# Revit family: Hager-Type B SP&N Distribution Boards-Surface_mounted-IP30-With_Cover-With_DIN-Hosted-GB-en
name_source: partatom
category: Electrical Equipment
units: mm (PartAtom-declared; Revit-internal decimal feet)

## family parameters
Cut with Voids When Loaded = No
Host = Face
Maintain Annotation Orientation = Yes
Panel Configuration = Two Columns, Circuits Across
Part Type = Panelboard
Room Calculation Point = No
Round Connector Dimension = Use Diameter
Shared = No

## types (4) — shared parameters
BC_MODEL_ID = 1554195
BC_OBJECT_ID = 513819
BC_OBJECT_VERSION = #1
Code hager = ADD-EC000214_EU
EF000003 - Mounting method = Surface mounted
EF000008 - Width = 465 mm  [stored 1.52559 ft]
EF000024 - UV resistant = No
EF000049 - Depth = 165 mm  [stored 0.541339 ft]
EF000116 - RAL number = 7035
EF000118 - With mounting plate = No
EF001062 - EMC-version = No
EF001088 - Extension possible = No
EF001134 - With DIN-rail = Yes
EF002950 - Width in number of modular spacings = 16
EF005474 - Degree of protection (IP rating) = IP30
EF006244 - Transparent cover/door = No
EF006306 - With lock = No
EF015776 - Earthing terminal block = Yes
EF015777 - Neutral terminal block = Yes
EF015941 - Signal passing door = No
ETIM class code = EC000214
ETIM class name = Small distribution board
HG000001-Number of columns = 1
HG000002-With door or cover = Yes
HG000003-Range = Type B SP&N Distribution Boards
HG000005-Thickness = 2 mm  [stored 0.00656168 ft]
HG000006-Flush mounted = No
HG000009-Double swing door = No
HG000010-Asymmetric doors = No
HG000011-Empty rows from bottom = No
HG000012-Door swing angle = 90.00°
HG000013-Door on the left = No
HG000014-Door on the right = Yes
HG000015-Clearance visibility = Yes
HG000016-Door 3D visibility = Yes
HG000017-Distance between poles = 18 mm  [stored 0.0590551 ft]
HG000060-RAL-number = 7035
HG000099-Onfly Template ID = 507532
HGEF002950-Width in number of modular spacings = 16
Manufacturer = Hager
Name = Type B SP&N Distribution Boards-Surface_mounted-IP30-With_Cover-With_DIN-GB
Name BIM&CO = Electricity
Name hager = ADD_Enclosures_EC000214
Uniformat = Low Tension Service & Dist.
Uniformat code = D501001
zero-valued in all types: Default Elevation, EF000218 - Recess depth, EF000332 - Recess height, EF000846 - Recess width, EF001131 - Internal depth, HG000007-Number of empty columns, HG000008-Number of empty rows

## per-type parameters (varying)
| type | BC_VARIANT_ID | EF000040 - Height | EF000266 - Number of rows | HG000004-Manufacturer reference | HGEF000266-Number of rows |
| Type B SP&N Distribution Boards-Surface_mounted_W465_H300_D165_16_Modular_Spacing-JK116E | 1178543 | 300 mm | 1 | JK116E | 1 |
| Type B SP&N Distribution Boards-Surface_mounted_W465_H300_D165_16_Modular_Spacing-JK116EG | 1178544 | 300 mm | 1 | JK116EG | 1 |
| Type B SP&N Distribution Boards-Surface_mounted_W465_H450_D165_16_Modular_Spacing-JK132E | 1178545 | 450 mm  [stored 1.47638 ft] | 2 | JK132E | 2 |
| Type B SP&N Distribution Boards-Surface_mounted_W465_H450_D165_16_Modular_Spacing-JK132EG | 1178546 | 450 mm  [stored 1.47638 ft] | 2 | JK132EG | 2 |

note: column(s) folded — value = type name in every type: Reference

note: [stored X ft] marks values corroborated as IEEE doubles in the binary element streams (Revit-internal decimal feet)

## geometry (parser evidence)
native form markers: Sweep x14
no freeform markers — native parametric forms only
